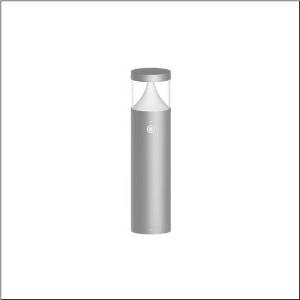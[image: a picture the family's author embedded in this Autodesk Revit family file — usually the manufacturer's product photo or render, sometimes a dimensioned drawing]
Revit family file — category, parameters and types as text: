
# Revit family: cl_31_poller_60_sensor_5cl434803
name_source: partatom
category: Lighting Fixtures
units: mm (PartAtom-declared; Revit-internal decimal feet)

## family parameters
Cut with Voids When Loaded = No
Host = Face
Light Source = No
Part Type = Normal
Room Calculation Point = No
Round Connector Dimension = Use Diameter
Shared = No

## types (1)
- --- (1 x LED, 1500 lm, 14 W, 3000K)
    Apparent Load = 14 VA
    CIE Flux Codes = 19 66 88 92 100
    Color Rendering = 80
    Color Temperature = 3000K
    Default Elevation = 1800 mm
    Description = CL 31 Bollard 60 Sensor, bollard luminaire, primary light control with lens, of PC, primary optical cover: cover panel, of PC, transparent, secondary light control with reflector, of PC, primary light characteristic: asymmetric, LED, rated luminous flux: 1.500lm, luminous efficacy: 107lm/W, light colour: 830, colour temperature: 3000K, control gear: ECG DALI, with terminal, 5-pole, max. 2.5mm², mains connection: 220..240V, AC, 50/60Hz, rated input power: 14W, luminaire housing, of aluminium, powder-coated, Siteco® metallic grey, diameter: 170mm, height: 600mm, PIR sensor, protection rating (complete): IP65, insulation class (complete): insulation class I (protective earthing), certification: CE, ENEC, impact resistance: IK08, permissible operating ambient temperature for outdoor applications: -20..+50°C, packaging unit: 1 piece
    Height = 200 mm  [stored 0.656168 ft]
    Lamp = 1 x LED
    Lamp Light Flux = 1500 lm
    Lamp Power = 14 W
    Lamp count = 1
    Length = 170 mm  [stored 0.557743 ft]
    Luminous efficacy = 107 lm/W
    Manufacturer = Siteco
    ModVariant = No
    Model = 5CL434803
    Mounting Place = Floor
    Mounting Type = Freestanding
    Number of Poles = 1
    OnlyDefault = Yes
    Power Factor = 1
    Product Name = CL 31 Poller 60 Sensor
    Product group = bollard luminaire | freestanding
    ProductGroupID = 1303
    Protection Class = Protection class I
    Protection Degree = IP 65
    RLX_Detail_Level = 1
    RlxData = <blob elided: 64657 chars, md5=27eb9595>
    Socket = socket
    Standby Power = 0 W
    System Light Flux = 1500 lm
    System Power = 14 W
    Type Comments = factory setting: luminous flux: 100 % | dim-lin: 254 | 350 mA
    Type Image = l_1006901.jpg
    URL = http://relux.com
    VarID = @adj_116897
    Voltage = 0 V
    Weight = 0.00 kg
    Width = 0 mm  [stored 0 ft]

note: [stored X ft] marks values corroborated as IEEE doubles in the binary element streams (Revit-internal decimal feet)

## geometry (parser evidence)
native form markers: Blend x4, Sweep x11
no freeform markers — native parametric forms only
